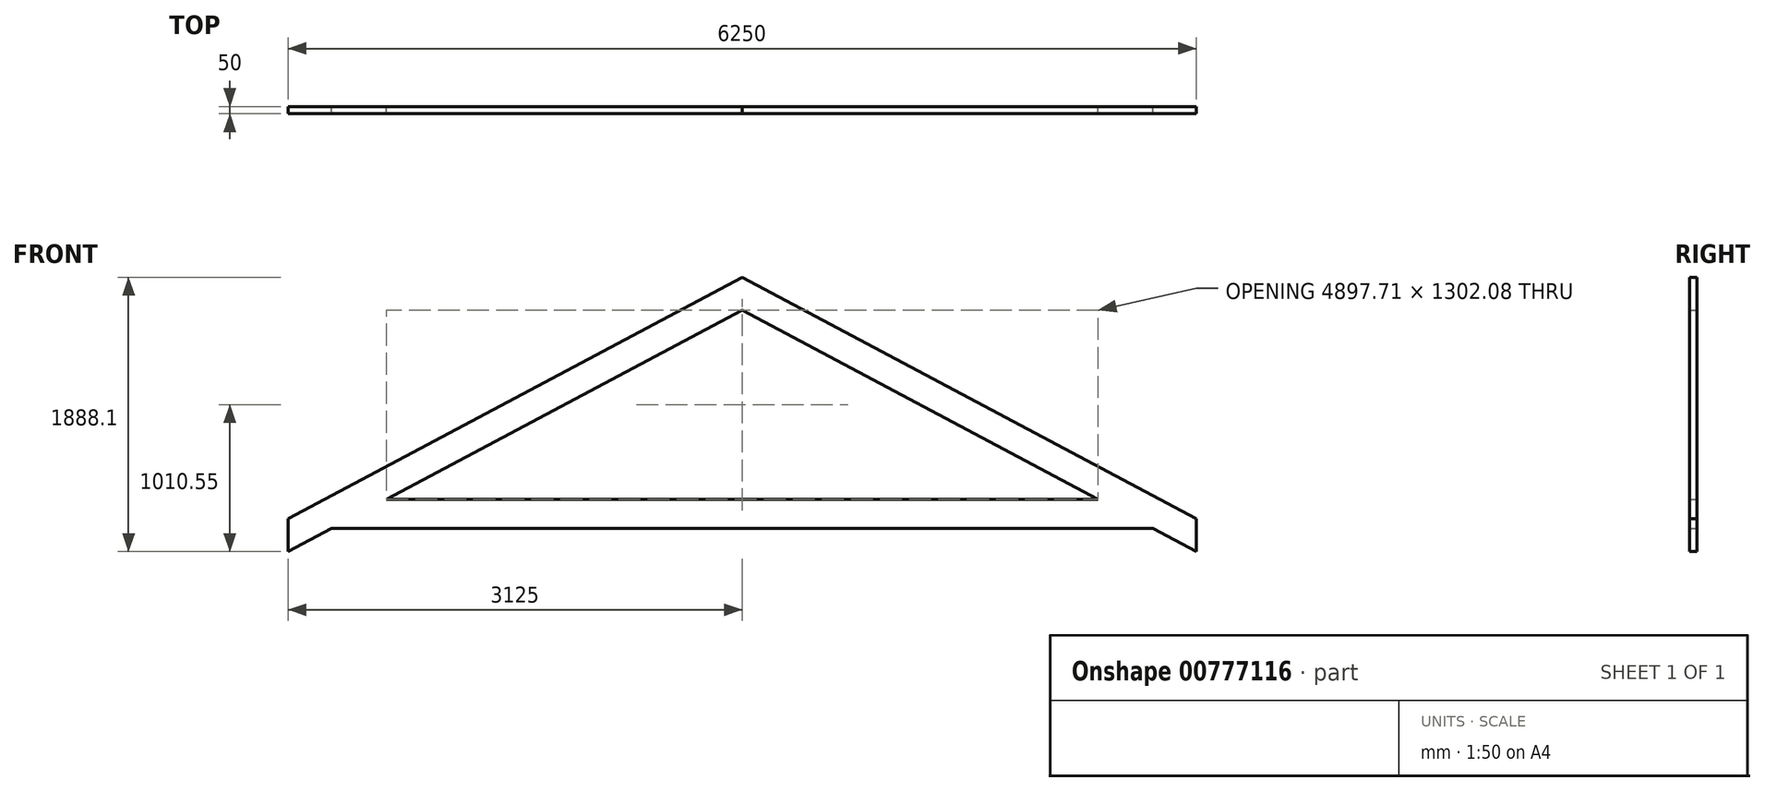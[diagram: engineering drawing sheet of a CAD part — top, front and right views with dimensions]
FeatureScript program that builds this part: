
annotation { "Feature Type Name" : "Feature", "Feature Type Description" : "" }
export const myFeature = defineFeature(function(context is Context, id is Id, definition is map)
    precondition{}
    {
        {
            var Q0;
            Q0=qCreatedBy(makeId("Front.planeOp"),FACE);
            var sketch = newSketch(context, id + "F0", { "sketchPlane" : qUnion([Q0])});
            skLineSegment(sketch, "E0.bottom", {"start": v(-2825, 100) * mm, "end": v(2825, 100) * mm});
            skPoint(sketch, "E0.middle", {"position": v(0, 0) * mm});
            skLineSegment(sketch, "E1", {"start": v(-3125, -59.51) * mm, "end": v(-2825, 100) * mm});
            skLineSegment(sketch, "E2", {"start": v(3125, -59.51) * mm, "end": v(2825, 100) * mm});
            skLineSegment(sketch, "E3.0", {"start": v(3125, 167) * mm, "end": v(0, 1828.6) * mm});
            skLineSegment(sketch, "E4.0", {"start": v(-3125, 167) * mm, "end": v(0, 1828.6) * mm});
            skLineSegment(sketch, "E5.0", {"start": v(3125, 167) * mm, "end": v(3125, -59.51) * mm});
            skLineSegment(sketch, "E5.2", {"start": v(-3125, 167) * mm, "end": v(-3125, -59.51) * mm});
            skLineSegment(sketch, "E6.trimOffspring", {"start": v(-2448.85, 300) * mm, "end": v(0, 1602.08) * mm});
            skLineSegment(sketch, "E7.trimOffspring", {"start": v(2448.85, 300) * mm, "end": v(0, 1602.08) * mm});
            skLineSegment(sketch, "E8.0", {"start": v(-2448.85, 300) * mm, "end": v(2448.85, 300) * mm});
            skSolve(sketch);
        }
        {
            var Q0;
            Q0=makeQuery(id+"F0.imprint","IMPRINT",FACE,{"disambiguationData":[TD([[makeQuery(id+"F0.imprint","IMPRINT",EDGE,{"derivedFrom":sQuery(id+"F0.wireOp",EDGE,"E3.0")}),1.0]])]});
            var Q1;
            Q1=makeQuery(id+"F0.imprint","IMPRINT",FACE,{"disambiguationData":[TD([[makeQuery(id+"F0.imprint","IMPRINT",EDGE,{"derivedFrom":sQuery(id+"F0.wireOp",EDGE,"E0.bottom")}),-1.0]])]});
            extrude(context, id + "F1", {"entities" : qUnion([Q0, Q1]), "depth" : 50 * mm, "offsetDistance" : 25 * mm});
        }
    });
